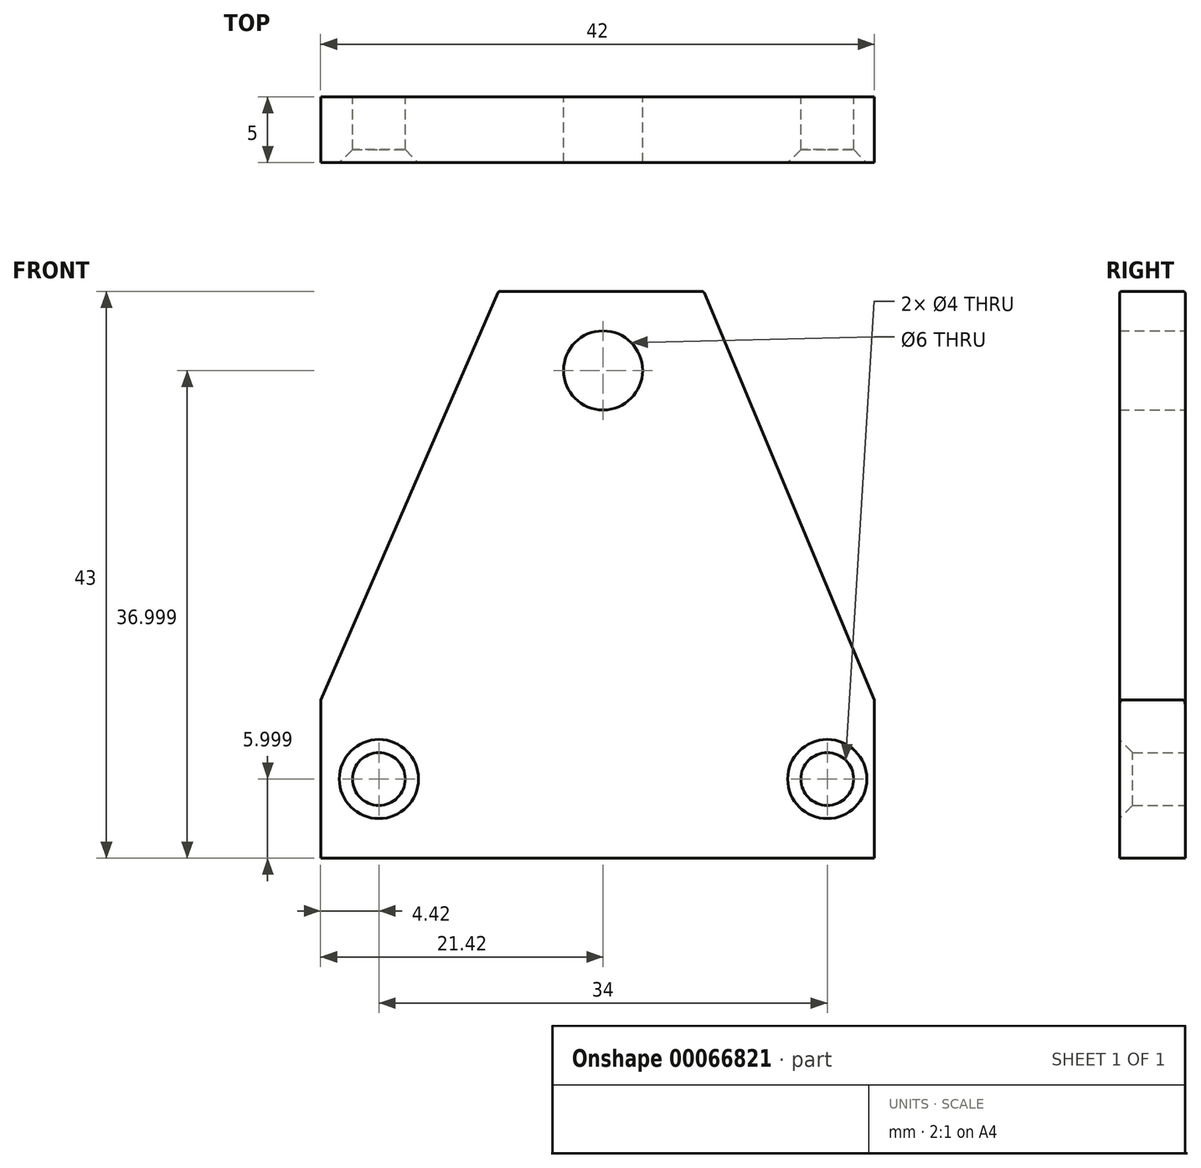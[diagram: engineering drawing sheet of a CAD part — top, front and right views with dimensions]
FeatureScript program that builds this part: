
annotation { "Feature Type Name" : "Feature", "Feature Type Description" : "" }
export const myFeature = defineFeature(function(context is Context, id is Id, definition is map)
    precondition{}
    {
        {
            var Q0;
            Q0=qCreatedBy(makeId("Front.planeOp"),FACE);
            var sketch = newSketch(context, id + "F0", { "sketchPlane" : qUnion([Q0])});
            skLineSegment(sketch, "E0.bottom", {"start": v(-21.42, -21.78) * mm, "end": v(20.58, -21.78) * mm});
            skLineSegment(sketch, "E0.top", {"start": v(-7.93, 21.22) * mm, "end": v(7.62, 21.22) * mm});
            skLineSegment(sketch, "E0.left", {"start": v(-21.42, -21.78) * mm, "end": v(-21.42, -9.78) * mm});
            skLineSegment(sketch, "E0.right", {"start": v(20.58, -21.78) * mm, "end": v(20.58, -9.78) * mm});
            skCircle(sketch, "E1", {"center": v(0, 15.22) * mm, "radius": 3 * mm});
            skLineSegment(sketch, "E2", {"start": v(-21.42, -9.78) * mm, "end": v(-7.93, 21.22) * mm});
            skLineSegment(sketch, "E3", {"start": v(7.62, 21.22) * mm, "end": v(20.58, -9.78) * mm});
            skPoint(sketch, "E4.orphan", {"position": v(0, 39.45) * mm});
            skPoint(sketch, "E5.orphan", {"position": v(20.58, 21.22) * mm});
            skPoint(sketch, "E6.trimOffspring.end.orphan", {"position": v(-21.42, 21.22) * mm});
            skPoint(sketch, "E7.left.start.orphan", {"position": v(-51.94, 15.22) * mm});
            skPoint(sketch, "E7.top.start.orphan", {"position": v(-51.94, -9.78) * mm});
            skCircle(sketch, "E8", {"center": v(-17, -15.78) * mm, "radius": 2 * mm});
            skCircle(sketch, "E9", {"center": v(17, -15.78) * mm, "radius": 2 * mm});
            skPoint(sketch, "E10.orphan", {"position": v(17, -21.78) * mm});
            skSolve(sketch);
        }
        {
            var Q0;
            Q0=makeQuery(id+"F0.imprint","IMPRINT",FACE,{"disambiguationData":[TD([[makeQuery(id+"F0.imprint","IMPRINT",EDGE,{"derivedFrom":sQuery(id+"F0.wireOp",EDGE,"E0.bottom")}),1.0]])]});
            extrude(context, id + "F1", {"entities" : qUnion([Q0]), "depth" : 5 * mm});
        }
        {
            var Q0;
            Q0=makeQuery(id+"F1.opExtrude","CAP_EDGE",EDGE,{"disambiguationData":[OSD([sQuery(id+"F0.wireOp",EDGE,"E2")])],"isStart":false});
            var Q1;
            Q1=makeQuery(id+"F1.opExtrude","CAP_EDGE",EDGE,{"disambiguationData":[OSD([sQuery(id+"F0.wireOp",EDGE,"E0.top")])],"isStart":false});
            var Q2;
            Q2=makeQuery(id+"F1.opExtrude","CAP_EDGE",EDGE,{"disambiguationData":[OSD([sQuery(id+"F0.wireOp",EDGE,"E3")])],"isStart":false});
            var Q3;
            Q3=makeQuery(id+"F1.opExtrude","CAP_EDGE",EDGE,{"disambiguationData":[OSD([sQuery(id+"F0.wireOp",EDGE,"E3")])],"isStart":true});
            var Q4;
            Q4=makeQuery(id+"F1.opExtrude","CAP_EDGE",EDGE,{"disambiguationData":[OSD([sQuery(id+"F0.wireOp",EDGE,"E0.top")])],"isStart":true});
            var Q5;
            Q5=makeQuery(id+"F1.opExtrude","SWEPT_EDGE",EDGE,{"disambiguationData":[OSD([sQuery(id+"F0.wireOp",EDGE,"E0.top"),sQuery(id+"F0.wireOp",EDGE,"E3")])]});
            var Q6;
            Q6=makeQuery(id+"F1.opExtrude","SWEPT_EDGE",EDGE,{"disambiguationData":[OSD([sQuery(id+"F0.wireOp",EDGE,"E0.top"),sQuery(id+"F0.wireOp",EDGE,"E2")])]});
            var Q7;
            Q7=makeQuery(id+"F1.opExtrude","CAP_EDGE",EDGE,{"disambiguationData":[OSD([sQuery(id+"F0.wireOp",EDGE,"E2")])],"isStart":true});
            fillet(context, id + "F2", {"entities" : qUnion([Q0, Q1, Q2, Q3, Q4, Q5, Q6, Q7]), "radius" : .2 * mm, "tangentPropagation" : true, "allowEdgeOverflow" : false});
        }
        {
            var Q0;
            Q0=makeQuery(id+"F1.opExtrude","CAP_EDGE",EDGE,{"disambiguationData":[OSD([sQuery(id+"F0.wireOp",EDGE,"E8")])],"isStart":false});
            var Q1;
            Q1=makeQuery(id+"F1.opExtrude","CAP_EDGE",EDGE,{"disambiguationData":[OSD([sQuery(id+"F0.wireOp",EDGE,"E9")])],"isStart":false});
            chamfer(context, id + "F3", {"entities" : qUnion([Q0, Q1]), "width" : 1 * mm, "tangentPropagation" : true});
        }
    });
